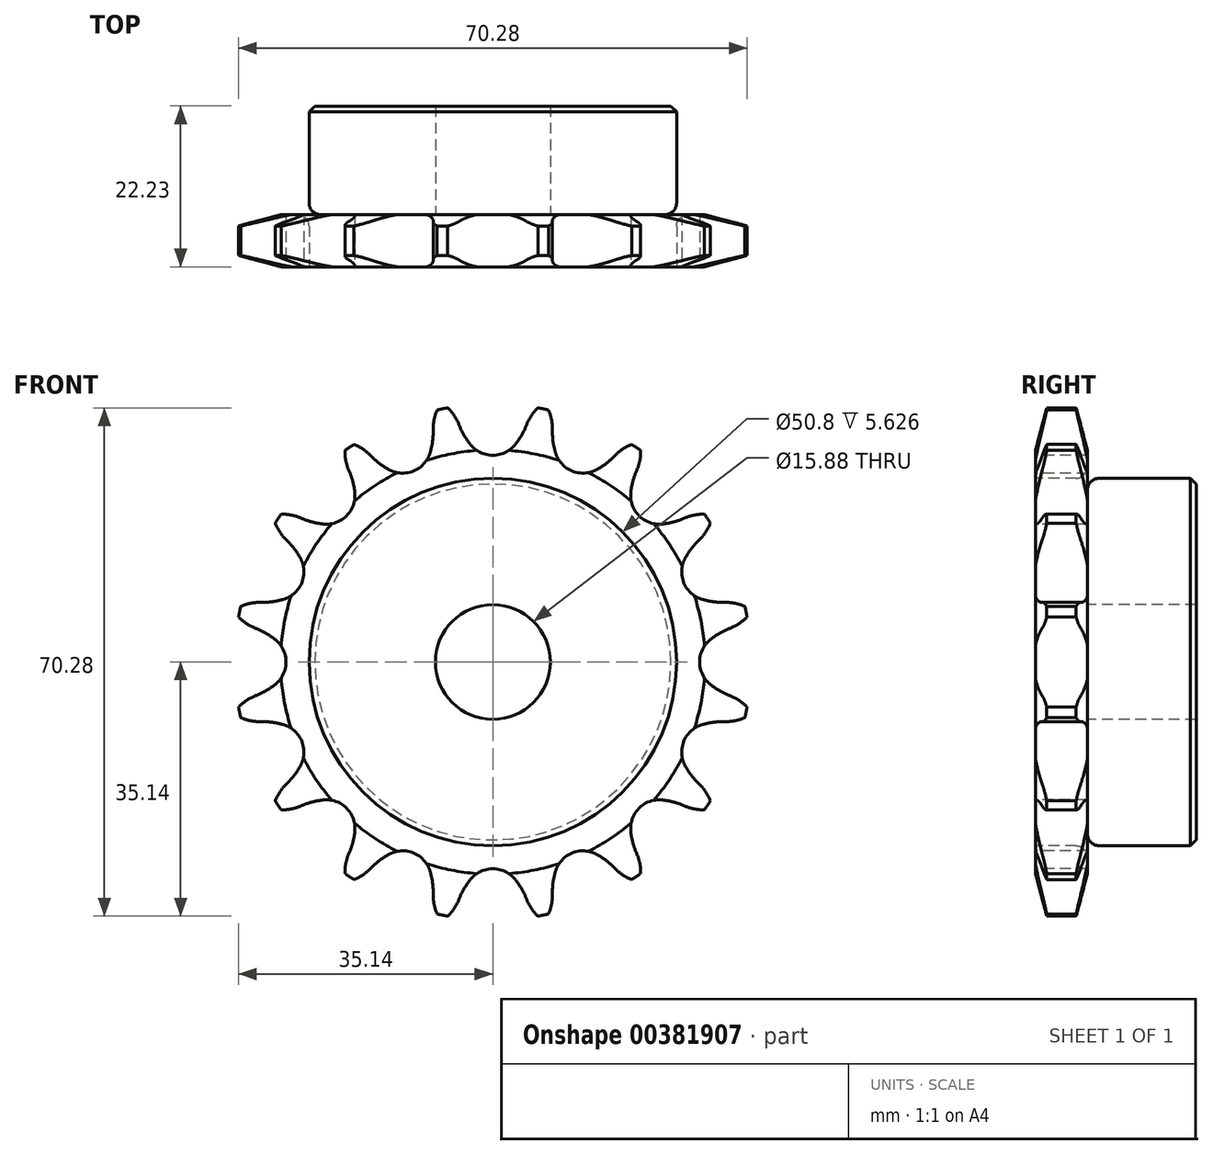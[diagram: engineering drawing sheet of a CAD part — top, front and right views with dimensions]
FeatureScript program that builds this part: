
annotation { "Feature Type Name" : "Feature", "Feature Type Description" : "" }
export const myFeature = defineFeature(function(context is Context, id is Id, definition is map)
    precondition{}
    {
        {
            var Q0;
            Q0=qCreatedBy(makeId("Right.planeOp"),FACE);
            var sketch = newSketch(context, id + "F0", { "sketchPlane" : qUnion([Q0])});
            skLineSegment(sketch, "E0", {"start": v(0, 0) * mm, "end": v(26.74, 0) * mm, "construction": true});
            skLineSegment(sketch, "E1.bottom", {"start": v(0, 7.94) * mm, "end": v(7.21, 7.94) * mm});
            skLineSegment(sketch, "E1.top", {"start": v(0, 35.69) * mm, "end": v(7.21, 35.69) * mm});
            skLineSegment(sketch, "E1.left", {"start": v(0, 7.94) * mm, "end": v(0, 35.69) * mm});
            skLineSegment(sketch, "E1.right", {"start": v(7.21, 7.94) * mm, "end": v(7.21, 35.69) * mm});
            skLineSegment(sketch, "E2.bottom", {"start": v(0, 7.94) * mm, "end": v(22.23, 7.94) * mm});
            skLineSegment(sketch, "E2.top", {"start": v(0, 25.4) * mm, "end": v(22.23, 25.4) * mm});
            skLineSegment(sketch, "E2.left", {"start": v(0, 7.94) * mm, "end": v(0, 25.4) * mm});
            skLineSegment(sketch, "E2.right", {"start": v(22.23, 7.94) * mm, "end": v(22.22, 25.4) * mm});
            skLineSegment(sketch, "E3.MirrorCS", {"start": v(0, -7.94) * mm, "end": v(7.21, -7.94) * mm});
            skLineSegment(sketch, "E4.MirrorCS", {"start": v(22.23, -7.94) * mm, "end": v(22.23, -25.4) * mm});
            skLineSegment(sketch, "E5.MirrorCS", {"start": v(0, -7.94) * mm, "end": v(0, -25.4) * mm});
            skLineSegment(sketch, "E6.MirrorCS", {"start": v(0, -35.69) * mm, "end": v(7.21, -35.69) * mm});
            skLineSegment(sketch, "E7.MirrorCS", {"start": v(0, -7.94) * mm, "end": v(0, -35.69) * mm});
            skLineSegment(sketch, "E8.MirrorCS", {"start": v(7.21, -7.94) * mm, "end": v(7.21, -35.69) * mm});
            skLineSegment(sketch, "E9.MirrorCS", {"start": v(0, -7.94) * mm, "end": v(22.23, -7.94) * mm});
            skLineSegment(sketch, "E10.MirrorCS", {"start": v(0, -25.4) * mm, "end": v(22.23, -25.4) * mm});
            skSolve(sketch);
        }
        {
            var Q0;
            {var subQ0=sQuery(id+"F0.wireOp",EDGE,"E1.top");Q0=makeQuery(id+"F0.imprint","IMPRINT",FACE,{"disambiguationData":[TD([[makeQuery(id+"F0.imprint","IMPRINT",EDGE,{"derivedFrom":subQ0}),-1.0]])]});}
            var Q1;
            {var subQ5=sQuery(id+"F0.wireOp",EDGE,"E2.left");Q1=makeQuery(id+"F0.imprint","IMPRINT",FACE,{"disambiguationData":[TD([[makeQuery(id+"F0.imprint","IMPRINT",EDGE,{"derivedFrom":subQ5}),-1.0]])]});}
            var Q2;
            {var subQ5=sQuery(id+"F0.wireOp",EDGE,"E2.right");Q2=makeQuery(id+"F0.imprint","IMPRINT",FACE,{"disambiguationData":[TD([[makeQuery(id+"F0.imprint","IMPRINT",EDGE,{"derivedFrom":subQ5}),1.0]])]});}
            var Q3;
            Q3=sQuery(id+"F0.wireOp",EDGE,"E0");
            revolve(context, id + "F1", {"entities" : qUnion([Q0, Q1, Q2]), "axis" : qUnion([Q3]), "revolveType" : RevolveType.FULL});
        }
        {
            var Q0;
            Q0=makeQuery(id+"F1.opRevolve","SWEPT_EDGE",EDGE,{"disambiguationData":[OSD([sQuery(id+"F0.wireOp",EDGE,"E1.right"),sQuery(id+"F0.wireOp",EDGE,"E2.top")])]});
            fillet(context, id + "F2", {"entities" : qUnion([Q0]), "radius" : 1.59 * mm, "tangentPropagation" : true, "allowEdgeOverflow" : false});
        }
        {
            var Q0;
            Q0=makeQuery(id+"F1.opRevolve","SWEPT_EDGE",EDGE,{"disambiguationData":[OSD([sQuery(id+"F0.wireOp",EDGE,"E2.top"),sQuery(id+"F0.wireOp",EDGE,"E2.right")])]});
            chamfer(context, id + "F3", {"entities" : qUnion([Q0]), "width" : 0.8 * mm, "tangentPropagation" : true});
        }
        {
            var Q0;
            Q0=makeQuery(id+"F1.opRevolve","SWEPT_FACE",FACE,{"disambiguationData":[OSD([sQuery(id+"F0.wireOp",EDGE,"E1.top")])]});
            chamfer(context, id + "F4", {"entities" : qUnion([Q0]), "chamferType" : ChamferType.TWO_OFFSETS, "width1" : 6.35 * mm, "oppositeDirection" : false, "width2" : 1.57 * mm, "tangentPropagation" : true});
        }
        {
            var Q0;
            Q0=makeQuery(id+"F1.opRevolve","SWEPT_FACE",FACE,{"disambiguationData":[OSD([sQuery(id+"F0.wireOp",EDGE,"E1.left"),sQuery(id+"F0.wireOp",EDGE,"E2.left")])]});
            var sketch = newSketch(context, id + "F5", { "sketchPlane" : qUnion([Q0])});
            skLineSegment(sketch, "E11", {"start": v(0, 0) * mm, "end": v(0, 32.55) * mm, "construction": true});
            skLineSegment(sketch, "E12", {"start": v(0, 32.55) * mm, "end": v(33.66, 32.55) * mm, "construction": true});
            skLineSegment(sketch, "E13", {"start": v(0, 32.55) * mm, "end": v(5, 36.56) * mm, "construction": true});
            skLineSegment(sketch, "E14", {"start": v(5, 36.56) * mm, "end": v(-3.9, 32.55) * mm, "construction": true});
            skLineSegment(sketch, "E15", {"start": v(3.62, 15.85) * mm, "end": v(-3.9, 32.55) * mm, "construction": true});
            skArc(sketch, "E16", {"start": v(-7.13, 35.87) * mm, "mid": v(-15.94, 26.26) * mm, "end": v(-4.66, 32.79) * mm, "construction": true});
            skArc(sketch, "E17", {"start": v(-4.66, 32.79) * mm, "mid": v(-5.66, 34.52) * mm, "end": v(-7.13, 35.87) * mm});
            skLineSegment(sketch, "E18", {"start": v(-4.66, 32.79) * mm, "end": v(-4.66, 32.79) * mm});
            skArc(sketch, "E19", {"start": v(-3.1, 30.07) * mm, "mid": v(-1.71, 28.98) * mm, "end": v(0, 28.59) * mm});
            skArc(sketch, "E20", {"start": v(-4.66, 32.79) * mm, "mid": v(-3.98, 31.37) * mm, "end": v(-3.1, 30.07) * mm});
            skArc(sketch, "E21.MirrorCS", {"start": v(4.66, 32.79) * mm, "mid": v(5.66, 34.52) * mm, "end": v(7.13, 35.87) * mm});
            skArc(sketch, "E22.MirrorCS", {"start": v(4.66, 32.79) * mm, "mid": v(3.98, 31.37) * mm, "end": v(3.1, 30.07) * mm});
            skArc(sketch, "E23.MirrorCS", {"start": v(3.1, 30.07) * mm, "mid": v(1.71, 28.98) * mm, "end": v(0, 28.59) * mm});
            skArc(sketch, "E24.1.0", {"start": v(-16.85, 28.5) * mm, "mid": v(-18.44, 29.72) * mm, "end": v(-20.32, 30.4) * mm});
            skArc(sketch, "E24.1.1", {"start": v(-16.85, 28.5) * mm, "mid": v(-15.68, 27.46) * mm, "end": v(-14.36, 26.6) * mm});
            skArc(sketch, "E24.1.2", {"start": v(-14.36, 26.6) * mm, "mid": v(-12.67, 26.12) * mm, "end": v(-10.94, 26.41) * mm});
            skArc(sketch, "E24.1.3", {"start": v(-8.65, 28.96) * mm, "mid": v(-9.5, 27.43) * mm, "end": v(-10.94, 26.41) * mm});
            skArc(sketch, "E24.1.4", {"start": v(-8.24, 32.08) * mm, "mid": v(-8.33, 30.5) * mm, "end": v(-8.65, 28.96) * mm});
            skArc(sketch, "E24.1.5", {"start": v(-8.24, 32.08) * mm, "mid": v(-7.98, 34.06) * mm, "end": v(-7.13, 35.87) * mm});
            skArc(sketch, "E24.2.0", {"start": v(-26.48, 19.89) * mm, "mid": v(-28.41, 20.4) * mm, "end": v(-30.4, 20.32) * mm});
            skArc(sketch, "E24.2.1", {"start": v(-26.48, 19.89) * mm, "mid": v(-25, 19.37) * mm, "end": v(-23.45, 19.08) * mm});
            skArc(sketch, "E24.2.2", {"start": v(-23.45, 19.08) * mm, "mid": v(-21.7, 19.28) * mm, "end": v(-20.21, 20.21) * mm});
            skArc(sketch, "E24.2.3", {"start": v(-19.08, 23.45) * mm, "mid": v(-19.28, 21.7) * mm, "end": v(-20.21, 20.21) * mm});
            skArc(sketch, "E24.2.4", {"start": v(-19.89, 26.48) * mm, "mid": v(-19.37, 25) * mm, "end": v(-19.08, 23.45) * mm});
            skArc(sketch, "E24.2.5", {"start": v(-19.89, 26.48) * mm, "mid": v(-20.4, 28.41) * mm, "end": v(-20.32, 30.4) * mm});
            skArc(sketch, "E24.3.0", {"start": v(-32.08, 8.24) * mm, "mid": v(-34.06, 7.98) * mm, "end": v(-35.87, 7.13) * mm});
            skArc(sketch, "E24.3.1", {"start": v(-32.08, 8.24) * mm, "mid": v(-30.5, 8.33) * mm, "end": v(-28.96, 8.65) * mm});
            skArc(sketch, "E24.3.2", {"start": v(-28.96, 8.65) * mm, "mid": v(-27.43, 9.5) * mm, "end": v(-26.41, 10.94) * mm});
            skArc(sketch, "E24.3.3", {"start": v(-26.6, 14.36) * mm, "mid": v(-26.12, 12.67) * mm, "end": v(-26.41, 10.94) * mm});
            skArc(sketch, "E24.3.4", {"start": v(-28.5, 16.85) * mm, "mid": v(-27.46, 15.68) * mm, "end": v(-26.6, 14.36) * mm});
            skArc(sketch, "E24.3.5", {"start": v(-28.5, 16.85) * mm, "mid": v(-29.72, 18.44) * mm, "end": v(-30.4, 20.32) * mm});
            skArc(sketch, "E24.4.0", {"start": v(-32.79, -4.66) * mm, "mid": v(-34.52, -5.66) * mm, "end": v(-35.87, -7.13) * mm});
            skArc(sketch, "E24.4.1", {"start": v(-32.79, -4.66) * mm, "mid": v(-31.37, -3.98) * mm, "end": v(-30.07, -3.1) * mm});
            skArc(sketch, "E24.4.2", {"start": v(-30.07, -3.1) * mm, "mid": v(-28.98, -1.71) * mm, "end": v(-28.59, 0) * mm});
            skArc(sketch, "E24.4.3", {"start": v(-30.07, 3.1) * mm, "mid": v(-28.98, 1.71) * mm, "end": v(-28.59, 0) * mm});
            skArc(sketch, "E24.4.4", {"start": v(-32.79, 4.66) * mm, "mid": v(-31.37, 3.98) * mm, "end": v(-30.07, 3.1) * mm});
            skArc(sketch, "E24.4.5", {"start": v(-32.79, 4.66) * mm, "mid": v(-34.52, 5.66) * mm, "end": v(-35.87, 7.13) * mm});
            skArc(sketch, "E24.5.0", {"start": v(-28.5, -16.85) * mm, "mid": v(-29.72, -18.44) * mm, "end": v(-30.4, -20.32) * mm});
            skArc(sketch, "E24.5.1", {"start": v(-28.5, -16.85) * mm, "mid": v(-27.46, -15.68) * mm, "end": v(-26.6, -14.36) * mm});
            skArc(sketch, "E24.5.2", {"start": v(-26.6, -14.36) * mm, "mid": v(-26.12, -12.67) * mm, "end": v(-26.41, -10.94) * mm});
            skArc(sketch, "E24.5.3", {"start": v(-28.96, -8.65) * mm, "mid": v(-27.43, -9.5) * mm, "end": v(-26.41, -10.94) * mm});
            skArc(sketch, "E24.5.4", {"start": v(-32.08, -8.24) * mm, "mid": v(-30.5, -8.33) * mm, "end": v(-28.96, -8.65) * mm});
            skArc(sketch, "E24.5.5", {"start": v(-32.08, -8.24) * mm, "mid": v(-34.06, -7.98) * mm, "end": v(-35.87, -7.13) * mm});
            skArc(sketch, "E24.6.0", {"start": v(-19.89, -26.48) * mm, "mid": v(-20.4, -28.41) * mm, "end": v(-20.32, -30.4) * mm});
            skArc(sketch, "E24.6.1", {"start": v(-19.89, -26.48) * mm, "mid": v(-19.37, -25) * mm, "end": v(-19.08, -23.45) * mm});
            skArc(sketch, "E24.6.2", {"start": v(-19.08, -23.45) * mm, "mid": v(-19.28, -21.7) * mm, "end": v(-20.21, -20.21) * mm});
            skArc(sketch, "E24.6.3", {"start": v(-23.45, -19.08) * mm, "mid": v(-21.7, -19.28) * mm, "end": v(-20.21, -20.21) * mm});
            skArc(sketch, "E24.6.4", {"start": v(-26.48, -19.89) * mm, "mid": v(-25, -19.37) * mm, "end": v(-23.45, -19.08) * mm});
            skArc(sketch, "E24.6.5", {"start": v(-26.48, -19.89) * mm, "mid": v(-28.41, -20.4) * mm, "end": v(-30.4, -20.32) * mm});
            skArc(sketch, "E24.7.0", {"start": v(-8.24, -32.08) * mm, "mid": v(-7.98, -34.06) * mm, "end": v(-7.13, -35.87) * mm});
            skArc(sketch, "E24.7.1", {"start": v(-8.24, -32.08) * mm, "mid": v(-8.33, -30.5) * mm, "end": v(-8.65, -28.96) * mm});
            skArc(sketch, "E24.7.2", {"start": v(-8.65, -28.96) * mm, "mid": v(-9.5, -27.43) * mm, "end": v(-10.94, -26.41) * mm});
            skArc(sketch, "E24.7.3", {"start": v(-14.36, -26.6) * mm, "mid": v(-12.67, -26.12) * mm, "end": v(-10.94, -26.41) * mm});
            skArc(sketch, "E24.7.4", {"start": v(-16.85, -28.5) * mm, "mid": v(-15.68, -27.46) * mm, "end": v(-14.36, -26.6) * mm});
            skArc(sketch, "E24.7.5", {"start": v(-16.85, -28.5) * mm, "mid": v(-18.44, -29.72) * mm, "end": v(-20.32, -30.4) * mm});
            skArc(sketch, "E24.8.0", {"start": v(4.66, -32.79) * mm, "mid": v(5.66, -34.52) * mm, "end": v(7.13, -35.87) * mm});
            skArc(sketch, "E24.8.1", {"start": v(4.66, -32.79) * mm, "mid": v(3.98, -31.37) * mm, "end": v(3.1, -30.07) * mm});
            skArc(sketch, "E24.8.2", {"start": v(3.1, -30.07) * mm, "mid": v(1.71, -28.98) * mm, "end": v(0, -28.59) * mm});
            skArc(sketch, "E24.8.3", {"start": v(-3.1, -30.07) * mm, "mid": v(-1.71, -28.98) * mm, "end": v(0, -28.59) * mm});
            skArc(sketch, "E24.8.4", {"start": v(-4.66, -32.79) * mm, "mid": v(-3.98, -31.37) * mm, "end": v(-3.1, -30.07) * mm});
            skArc(sketch, "E24.8.5", {"start": v(-4.66, -32.79) * mm, "mid": v(-5.66, -34.52) * mm, "end": v(-7.13, -35.87) * mm});
            skArc(sketch, "E24.9.0", {"start": v(16.85, -28.5) * mm, "mid": v(18.44, -29.72) * mm, "end": v(20.32, -30.4) * mm});
            skArc(sketch, "E24.9.1", {"start": v(16.85, -28.5) * mm, "mid": v(15.68, -27.46) * mm, "end": v(14.36, -26.6) * mm});
            skArc(sketch, "E24.9.2", {"start": v(14.36, -26.6) * mm, "mid": v(12.67, -26.12) * mm, "end": v(10.94, -26.41) * mm});
            skArc(sketch, "E24.9.3", {"start": v(8.65, -28.96) * mm, "mid": v(9.5, -27.43) * mm, "end": v(10.94, -26.41) * mm});
            skArc(sketch, "E24.9.4", {"start": v(8.24, -32.08) * mm, "mid": v(8.33, -30.5) * mm, "end": v(8.65, -28.96) * mm});
            skArc(sketch, "E24.9.5", {"start": v(8.24, -32.08) * mm, "mid": v(7.98, -34.06) * mm, "end": v(7.13, -35.87) * mm});
            skArc(sketch, "E24.10.0", {"start": v(26.48, -19.89) * mm, "mid": v(28.41, -20.4) * mm, "end": v(30.4, -20.32) * mm});
            skArc(sketch, "E24.10.1", {"start": v(26.48, -19.89) * mm, "mid": v(25, -19.37) * mm, "end": v(23.45, -19.08) * mm});
            skArc(sketch, "E24.10.2", {"start": v(23.45, -19.08) * mm, "mid": v(21.7, -19.28) * mm, "end": v(20.21, -20.21) * mm});
            skArc(sketch, "E24.10.3", {"start": v(19.08, -23.45) * mm, "mid": v(19.28, -21.7) * mm, "end": v(20.21, -20.21) * mm});
            skArc(sketch, "E24.10.4", {"start": v(19.89, -26.48) * mm, "mid": v(19.37, -25) * mm, "end": v(19.08, -23.45) * mm});
            skArc(sketch, "E24.10.5", {"start": v(19.89, -26.48) * mm, "mid": v(20.4, -28.41) * mm, "end": v(20.32, -30.4) * mm});
            skArc(sketch, "E24.11.0", {"start": v(32.08, -8.24) * mm, "mid": v(34.06, -7.98) * mm, "end": v(35.87, -7.13) * mm});
            skArc(sketch, "E24.11.1", {"start": v(32.08, -8.24) * mm, "mid": v(30.5, -8.33) * mm, "end": v(28.96, -8.65) * mm});
            skArc(sketch, "E24.11.2", {"start": v(28.96, -8.65) * mm, "mid": v(27.43, -9.5) * mm, "end": v(26.41, -10.94) * mm});
            skArc(sketch, "E24.11.3", {"start": v(26.6, -14.36) * mm, "mid": v(26.12, -12.67) * mm, "end": v(26.41, -10.94) * mm});
            skArc(sketch, "E24.11.4", {"start": v(28.5, -16.85) * mm, "mid": v(27.46, -15.68) * mm, "end": v(26.6, -14.36) * mm});
            skArc(sketch, "E24.11.5", {"start": v(28.5, -16.85) * mm, "mid": v(29.72, -18.44) * mm, "end": v(30.4, -20.32) * mm});
            skArc(sketch, "E24.12.0", {"start": v(32.79, 4.66) * mm, "mid": v(34.52, 5.66) * mm, "end": v(35.87, 7.13) * mm});
            skArc(sketch, "E24.12.1", {"start": v(32.79, 4.66) * mm, "mid": v(31.37, 3.98) * mm, "end": v(30.07, 3.1) * mm});
            skArc(sketch, "E24.12.2", {"start": v(30.07, 3.1) * mm, "mid": v(28.98, 1.71) * mm, "end": v(28.59, 0) * mm});
            skArc(sketch, "E24.12.3", {"start": v(30.07, -3.1) * mm, "mid": v(28.98, -1.71) * mm, "end": v(28.59, 0) * mm});
            skArc(sketch, "E24.12.4", {"start": v(32.79, -4.66) * mm, "mid": v(31.37, -3.98) * mm, "end": v(30.07, -3.1) * mm});
            skArc(sketch, "E24.12.5", {"start": v(32.79, -4.66) * mm, "mid": v(34.52, -5.66) * mm, "end": v(35.87, -7.13) * mm});
            skArc(sketch, "E24.13.0", {"start": v(28.5, 16.85) * mm, "mid": v(29.72, 18.44) * mm, "end": v(30.4, 20.32) * mm});
            skArc(sketch, "E24.13.1", {"start": v(28.5, 16.85) * mm, "mid": v(27.46, 15.68) * mm, "end": v(26.6, 14.36) * mm});
            skArc(sketch, "E24.13.2", {"start": v(26.6, 14.36) * mm, "mid": v(26.12, 12.67) * mm, "end": v(26.41, 10.94) * mm});
            skArc(sketch, "E24.13.3", {"start": v(28.96, 8.65) * mm, "mid": v(27.43, 9.5) * mm, "end": v(26.41, 10.94) * mm});
            skArc(sketch, "E24.13.4", {"start": v(32.08, 8.24) * mm, "mid": v(30.5, 8.33) * mm, "end": v(28.96, 8.65) * mm});
            skArc(sketch, "E24.13.5", {"start": v(32.08, 8.24) * mm, "mid": v(34.06, 7.98) * mm, "end": v(35.87, 7.13) * mm});
            skArc(sketch, "E24.14.0", {"start": v(19.89, 26.48) * mm, "mid": v(20.4, 28.41) * mm, "end": v(20.32, 30.4) * mm});
            skArc(sketch, "E24.14.1", {"start": v(19.89, 26.48) * mm, "mid": v(19.37, 25) * mm, "end": v(19.08, 23.45) * mm});
            skArc(sketch, "E24.14.2", {"start": v(19.08, 23.45) * mm, "mid": v(19.28, 21.7) * mm, "end": v(20.21, 20.21) * mm});
            skArc(sketch, "E24.14.3", {"start": v(23.45, 19.08) * mm, "mid": v(21.7, 19.28) * mm, "end": v(20.21, 20.21) * mm});
            skArc(sketch, "E24.14.4", {"start": v(26.48, 19.89) * mm, "mid": v(25, 19.37) * mm, "end": v(23.45, 19.08) * mm});
            skArc(sketch, "E24.14.5", {"start": v(26.48, 19.89) * mm, "mid": v(28.41, 20.4) * mm, "end": v(30.4, 20.32) * mm});
            skArc(sketch, "E24.15.0", {"start": v(8.24, 32.08) * mm, "mid": v(7.98, 34.06) * mm, "end": v(7.13, 35.87) * mm});
            skArc(sketch, "E24.15.1", {"start": v(8.24, 32.08) * mm, "mid": v(8.33, 30.5) * mm, "end": v(8.65, 28.96) * mm});
            skArc(sketch, "E24.15.2", {"start": v(8.65, 28.96) * mm, "mid": v(9.5, 27.43) * mm, "end": v(10.94, 26.41) * mm});
            skArc(sketch, "E24.15.3", {"start": v(14.36, 26.6) * mm, "mid": v(12.67, 26.12) * mm, "end": v(10.94, 26.41) * mm});
            skArc(sketch, "E24.15.4", {"start": v(16.85, 28.5) * mm, "mid": v(15.68, 27.46) * mm, "end": v(14.36, 26.6) * mm});
            skArc(sketch, "E24.15.5", {"start": v(16.85, 28.5) * mm, "mid": v(18.44, 29.72) * mm, "end": v(20.32, 30.4) * mm});
            skPoint(sketch, "E24.center", {"position": v(0, 0) * mm});
            skSolve(sketch);
        }
        {
            var Q0;
            Q0 = qSketchRegion(id + "F5", true);
            extrude(context, id + "F6", {"entities" : qUnion([Q0]), "operationType" : NewBodyOperationType.INTERSECT, "endBound" : BoundingType.THROUGH_ALL, "oppositeDirection" : true, "depth" : 25.4 * mm});
        }
    });
